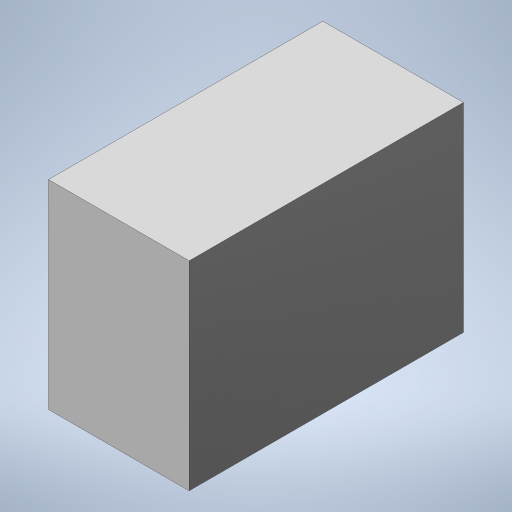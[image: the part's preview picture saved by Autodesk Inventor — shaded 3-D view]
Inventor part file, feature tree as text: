
AUTODESK INVENTOR PART (.ipt)
format: ipt  version: 2023 (Build 270158000, 158)  size: 198,656 bytes
history: native  units: mm
features: extrude x2, sketch x2, projected_geometry x1
ambient origin geometry x8: Origin, YZ Plane, XZ Plane, XY Plane, X Axis, Y Axis, Z Axis, Center Point
bodies: 实体1 (feature_tree)
feature tree (5):
  extrude  "拉伸1"  Depth=850.0mm
  extrude  "拉伸2"  Depth=600.0mm TaperAngle=0.0deg
  sketch  "草图1"  dims[d0=850.0mm d1=1200.0mm]
  sketch  "草图2"  dims[d2=600.0mm d3=0.0mm d4=30.0mm d5=0.0mm]
  projected_geometry  "投影回路1"
